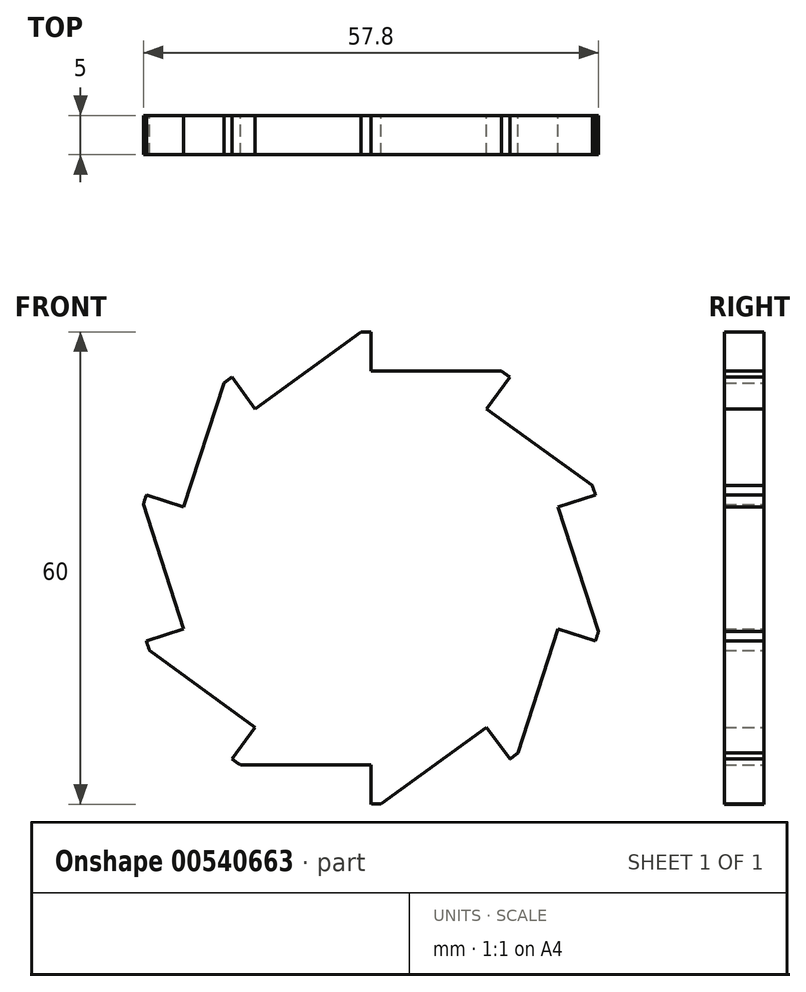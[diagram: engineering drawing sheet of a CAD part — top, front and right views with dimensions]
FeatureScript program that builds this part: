
annotation { "Feature Type Name" : "Feature", "Feature Type Description" : "" }
export const myFeature = defineFeature(function(context is Context, id is Id, definition is map)
    precondition{}
    {
        {
            var Q0;
            Q0=qCreatedBy(makeId("Front.planeOp"),FACE);
            var sketch = newSketch(context, id + "F0", { "sketchPlane" : qUnion([Q0])});
            skCircle(sketch, "E0", {"center": v(0, 0) * mm, "radius": 30 * mm});
            skLineSegment(sketch, "E1", {"start": v(0, 25) * mm, "end": v(16.58, 25) * mm});
            skLineSegment(sketch, "E2", {"start": v(0, 25) * mm, "end": v(0, 30) * mm});
            skLineSegment(sketch, "E3.1.0", {"start": v(-14.7, 20.23) * mm, "end": v(-17.63, 24.27) * mm});
            skLineSegment(sketch, "E3.1.1", {"start": v(-14.7, 20.23) * mm, "end": v(-1.28, 29.97) * mm});
            skLineSegment(sketch, "E3.2.0", {"start": v(-23.78, 7.73) * mm, "end": v(-28.53, 9.27) * mm});
            skLineSegment(sketch, "E3.2.1", {"start": v(-23.78, 7.73) * mm, "end": v(-18.65, 23.5) * mm});
            skLineSegment(sketch, "E3.3.0", {"start": v(-23.78, -7.73) * mm, "end": v(-28.53, -9.27) * mm});
            skLineSegment(sketch, "E3.3.1", {"start": v(-23.78, -7.73) * mm, "end": v(-28.9, 8.05) * mm});
            skLineSegment(sketch, "E3.4.0", {"start": v(-14.7, -20.23) * mm, "end": v(-17.63, -24.27) * mm});
            skLineSegment(sketch, "E3.4.1", {"start": v(-14.7, -20.23) * mm, "end": v(-28.11, -10.48) * mm});
            skLineSegment(sketch, "E3.5.0", {"start": v(0, -25) * mm, "end": v(0, -30) * mm});
            skLineSegment(sketch, "E3.5.1", {"start": v(0, -25) * mm, "end": v(-16.58, -25) * mm});
            skLineSegment(sketch, "E3.6.0", {"start": v(14.7, -20.23) * mm, "end": v(17.63, -24.27) * mm});
            skLineSegment(sketch, "E3.6.1", {"start": v(14.7, -20.23) * mm, "end": v(1.28, -29.97) * mm});
            skLineSegment(sketch, "E3.7.0", {"start": v(23.78, -7.73) * mm, "end": v(28.53, -9.27) * mm});
            skLineSegment(sketch, "E3.7.1", {"start": v(23.78, -7.73) * mm, "end": v(18.65, -23.5) * mm});
            skLineSegment(sketch, "E3.8.0", {"start": v(23.78, 7.73) * mm, "end": v(28.53, 9.27) * mm});
            skLineSegment(sketch, "E3.8.1", {"start": v(23.78, 7.73) * mm, "end": v(28.9, -8.05) * mm});
            skLineSegment(sketch, "E3.9.0", {"start": v(14.7, 20.23) * mm, "end": v(17.63, 24.27) * mm});
            skLineSegment(sketch, "E3.9.1", {"start": v(14.7, 20.23) * mm, "end": v(28.11, 10.48) * mm});
            skSolve(sketch);
        }
        {
            var Q0;
            {var subQ15=sQuery(id+"F0.wireOp",EDGE,"E1");Q0=makeQuery(id+"F0.imprint","IMPRINT",FACE,{"disambiguationData":[TD([[makeQuery(id+"F0.imprint","IMPRINT",EDGE,{"derivedFrom":subQ15}),-1.0]])]});}
            extrude(context, id + "F1", {"entities" : qUnion([Q0]), "depth" : 5 * mm, "offsetDistance" : 25 * mm});
        }
    });
